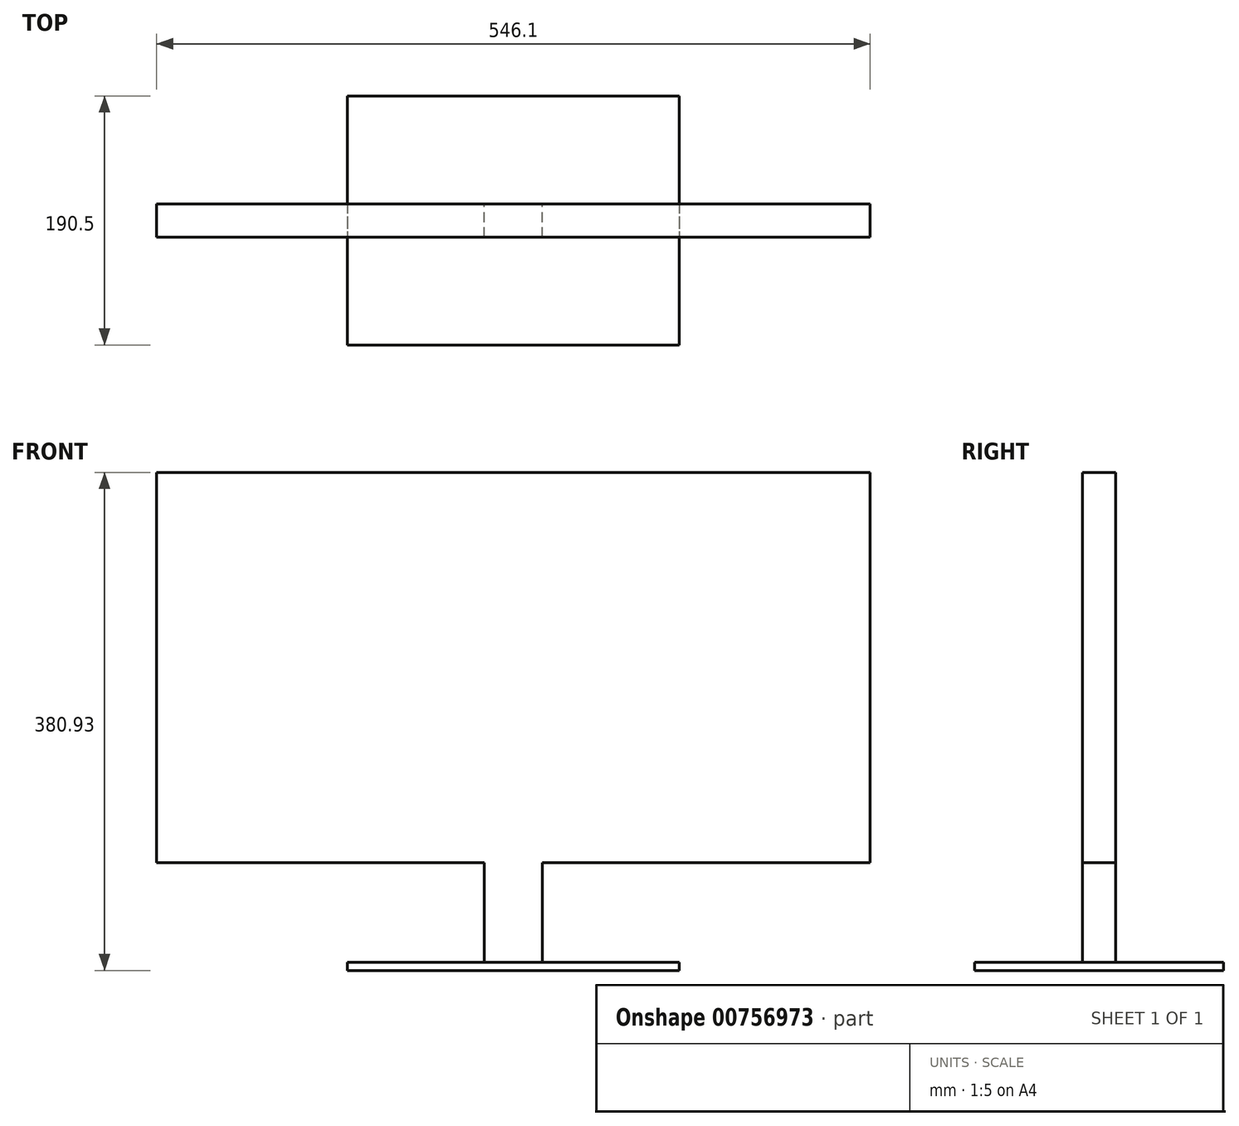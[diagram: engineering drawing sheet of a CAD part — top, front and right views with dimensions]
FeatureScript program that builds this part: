
annotation { "Feature Type Name" : "Feature", "Feature Type Description" : "" }
export const myFeature = defineFeature(function(context is Context, id is Id, definition is map)
    precondition{}
    {
        {
            var Q0;
            Q0=qCreatedBy(makeId("Front.planeOp"),FACE);
            var sketch = newSketch(context, id + "F0", { "sketchPlane" : qUnion([Q0])});
            skLineSegment(sketch, "E0.bottom", {"start": v(273.05, 149.2) * mm, "end": v(-273.05, 149.2) * mm});
            skLineSegment(sketch, "E0.top", {"start": v(273.05, -149.2) * mm, "end": v(-273.05, -149.2) * mm});
            skLineSegment(sketch, "E0.left", {"start": v(273.05, 149.2) * mm, "end": v(273.05, -149.2) * mm});
            skLineSegment(sketch, "E0.right", {"start": v(-273.05, 149.2) * mm, "end": v(-273.05, -149.2) * mm});
            skPoint(sketch, "E0.middle", {"position": v(0, 0) * mm});
            skLineSegment(sketch, "E1", {"start": v(-273.05, 149.2) * mm, "end": v(273.05, -149.2) * mm});
            skLineSegment(sketch, "E2.top", {"start": v(22.23, -225.4) * mm, "end": v(-22.22, -225.4) * mm});
            skLineSegment(sketch, "E2.left", {"start": v(22.23, -149.2) * mm, "end": v(22.23, -225.4) * mm});
            skLineSegment(sketch, "E2.right", {"start": v(-22.22, -149.2) * mm, "end": v(-22.22, -225.4) * mm});
            skPoint(sketch, "E2.middle", {"position": v(0, -149.2) * mm});
            skSolve(sketch);
        }
        {
            var Q0;
            Q0=qSketchRegion(id+"F0",true);
            extrude(context, id + "F1", {"entities" : qUnion([Q0]), "endBound" : BoundingType.SYMMETRIC, "depth" : 25.4 * mm});
        }
        {
            var Q0;
            Q0=makeQuery(id+"F1.opExtrude","SWEPT_FACE",FACE,{"disambiguationData":[OSD([sQuery(id+"F0.wireOp",EDGE,"E2.top")])]});
            var sketch = newSketch(context, id + "F2", { "sketchPlane" : qUnion([Q0])});
            skLineSegment(sketch, "E3.bottom", {"start": v(127, -95.25) * mm, "end": v(-127, -95.25) * mm});
            skLineSegment(sketch, "E3.top", {"start": v(127, 95.25) * mm, "end": v(-127, 95.25) * mm});
            skLineSegment(sketch, "E3.left", {"start": v(127, -95.25) * mm, "end": v(127, 95.25) * mm});
            skLineSegment(sketch, "E3.right", {"start": v(-127, -95.25) * mm, "end": v(-127, 95.25) * mm});
            skPoint(sketch, "E3.middle", {"position": v(0, 0) * mm});
            skSolve(sketch);
        }
        {
            var Q0;
            Q0=qSketchRegion(id+"F2",true);
            extrude(context, id + "F3", {"entities" : qUnion([Q0]), "operationType" : NewBodyOperationType.ADD, "depth" : 6.35 * mm});
        }
    });
